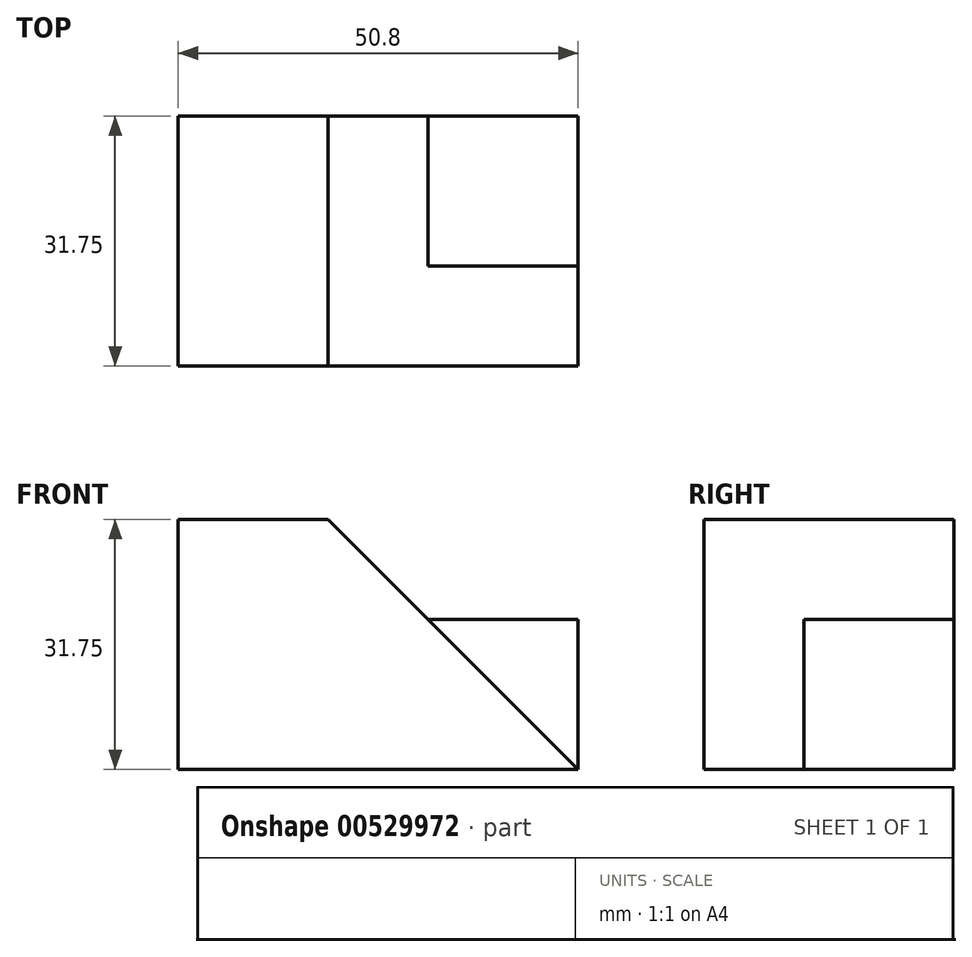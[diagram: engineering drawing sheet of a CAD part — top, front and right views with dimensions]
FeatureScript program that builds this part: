
annotation { "Feature Type Name" : "Feature", "Feature Type Description" : "" }
export const myFeature = defineFeature(function(context is Context, id is Id, definition is map)
    precondition{}
    {
        {
            var Q0;
            Q0=qCreatedBy(makeId("Front.planeOp"),FACE);
            var sketch = newSketch(context, id + "F0", { "sketchPlane" : qUnion([Q0])});
            skLineSegment(sketch, "E0", {"start": v(-60.58, 38.06) * mm, "end": v(-60.58, 6.3) * mm});
            skLineSegment(sketch, "E1", {"start": v(-60.58, 6.3) * mm, "end": v(-9.78, 6.3) * mm});
            skLineSegment(sketch, "E2", {"start": v(-9.78, 6.3) * mm, "end": v(-9.78, 25.36) * mm});
            skLineSegment(sketch, "E3", {"start": v(-9.78, 25.36) * mm, "end": v(-28.83, 25.36) * mm});
            skLineSegment(sketch, "E4", {"start": v(-60.58, 38.06) * mm, "end": v(-41.53, 38.06) * mm});
            skLineSegment(sketch, "E5", {"start": v(-28.83, 25.36) * mm, "end": v(-41.53, 38.06) * mm});
            skSolve(sketch);
        }
        {
            var Q0;
            Q0=makeQuery(id+"F0.imprint","IMPRINT",FACE,{"disambiguationData":[TD([[makeQuery(id+"F0.imprint","IMPRINT",EDGE,{"derivedFrom":sQuery(id+"F0.wireOp",EDGE,"E0")}),1.0]])]});
            extrude(context, id + "F1", {"entities" : qUnion([Q0]), "depth" : 31.75 * mm, "offsetDistance" : 25.4 * mm});
        }
        {
            var Q0;
            Q0=makeQuery(id+"F1.opExtrude","CAP_FACE",FACE,{"disambiguationData":[OSD([sQuery(id+"F0.wireOp",EDGE,"E0"),sQuery(id+"F0.wireOp",EDGE,"E1"),sQuery(id+"F0.wireOp",EDGE,"E2"),sQuery(id+"F0.wireOp",EDGE,"E3"),sQuery(id+"F0.wireOp",EDGE,"E4"),sQuery(id+"F0.wireOp",EDGE,"E5")])],"isStart":false});
            var sketch = newSketch(context, id + "F2", { "sketchPlane" : qUnion([Q0])});
            skLineSegment(sketch, "E6", {"start": v(-28.83, 25.36) * mm, "end": v(-9.78, 6.3) * mm});
            skSolve(sketch);
        }
        {
            var Q0;
            Q0=makeQuery(id+"F2.imprint","IMPRINT",FACE,{"disambiguationData":[TD([[makeQuery(id+"F2.imprint","IMPRINT",EDGE,{"derivedFrom":sQuery(id+"F2.wireOp",EDGE,"E6")}),1.0]])]});
            extrude(context, id + "F3", {"entities" : qUnion([Q0]), "operationType" : NewBodyOperationType.REMOVE, "oppositeDirection" : true, "depth" : 12.7 * mm, "offsetDistance" : 25.4 * mm});
        }
    });
